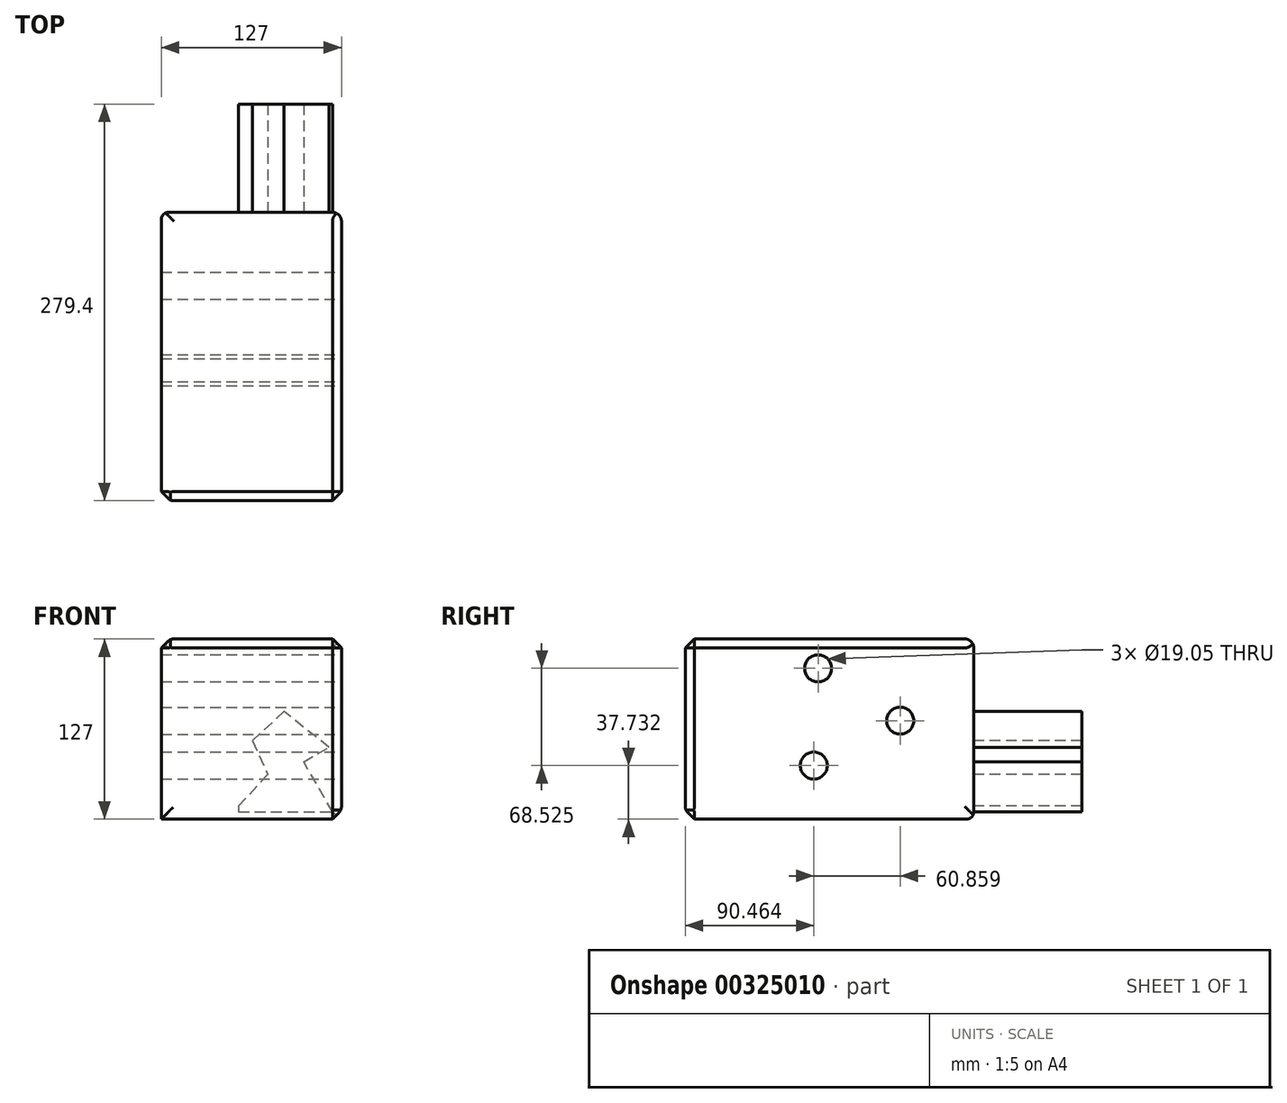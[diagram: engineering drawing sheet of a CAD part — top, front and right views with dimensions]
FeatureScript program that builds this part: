
annotation { "Feature Type Name" : "Feature", "Feature Type Description" : "" }
export const myFeature = defineFeature(function(context is Context, id is Id, definition is map)
    precondition{}
    {
        {
            var Q0;
            Q0=qCreatedBy(makeId("Front.planeOp"),FACE);
            var sketch = newSketch(context, id + "F0", { "sketchPlane" : qUnion([Q0])});
            skLineSegment(sketch, "E0.bottom", {"start": v(0, 0) * mm, "end": v(127, 0) * mm});
            skLineSegment(sketch, "E0.top", {"start": v(0, 127) * mm, "end": v(127, 127) * mm});
            skLineSegment(sketch, "E0.left", {"start": v(0, 0) * mm, "end": v(0, 127) * mm});
            skLineSegment(sketch, "E0.right", {"start": v(127, 0) * mm, "end": v(127, 127) * mm});
            skSolve(sketch);
        }
        {
            var Q0;
            Q0=makeQuery(id+"F0.imprint","IMPRINT",FACE,{"disambiguationData":[TD([[makeQuery(id+"F0.imprint","IMPRINT",EDGE,{"derivedFrom":sQuery(id+"F0.wireOp",EDGE,"E0.bottom")}),1.0]])]});
            extrude(context, id + "F1", {"entities" : qUnion([Q0]), "depth" : 203.2 * mm});
        }
        {
            var Q0;
            Q0=makeQuery(id+"F1.opExtrude","SWEPT_FACE",FACE,{"disambiguationData":[OSD([sQuery(id+"F0.wireOp",EDGE,"E0.right")])]});
            var sketch = newSketch(context, id + "F2", { "sketchPlane" : qUnion([Q0])});
            skCircle(sketch, "E1", {"center": v(-109.7, 106.26) * mm, "radius": 7.62 * mm});
            skCircle(sketch, "E2.1.0", {"center": v(-112.74, 37.73) * mm, "radius": 7.62 * mm});
            skCircle(sketch, "E2.2.0", {"center": v(-51.88, 69.37) * mm, "radius": 7.62 * mm});
            skPoint(sketch, "E2.center", {"position": v(-91.44, 71.12) * mm});
            skSolve(sketch);
        }
        {
            var Q0;
            Q0=sQuery(id+"F2.wireOp",VERTEX,"E1.center");
            var Q1;
            Q1=sQuery(id+"F2.wireOp",VERTEX,"E2.2.0.center");
            var Q2;
            Q2=sQuery(id+"F2.wireOp",VERTEX,"E2.1.0.center");
            var Q3;
            Q3=makeQuery(id+"F1.opExtrude","SWEPT_BODY",BODY,{"disambiguationData":[OSD([sQuery(id+"F0.wireOp",EDGE,"E0.bottom"),sQuery(id+"F0.wireOp",EDGE,"E0.top"),sQuery(id+"F0.wireOp",EDGE,"E0.left"),sQuery(id+"F0.wireOp",EDGE,"E0.right")])]});
            hole(context, id + "F3", {"style" : HoleStyle.SIMPLE, "endStyle" : HoleEndStyle.THROUGH, "holeDiameter" : 19.05 * mm, "tappedDepth" : 12.7 * mm, "tapClearance" : 3, "locations" : qUnion([Q0, Q1, Q2]), "scope" : qUnion([Q3])});
        }
        {
            var Q0;
            Q0=makeQuery(id+"F1.opExtrude","CAP_EDGE",EDGE,{"disambiguationData":[OSD([sQuery(id+"F0.wireOp",EDGE,"E0.top")])],"isStart":false});
            var Q1;
            Q1=makeQuery(id+"F1.opExtrude","CAP_EDGE",EDGE,{"disambiguationData":[OSD([sQuery(id+"F0.wireOp",EDGE,"E0.left")])],"isStart":false});
            var Q2;
            Q2=makeQuery(id+"F1.opExtrude","CAP_EDGE",EDGE,{"disambiguationData":[OSD([sQuery(id+"F0.wireOp",EDGE,"E0.right")])],"isStart":false});
            var Q3;
            Q3=makeQuery(id+"F1.opExtrude","CAP_EDGE",EDGE,{"disambiguationData":[OSD([sQuery(id+"F0.wireOp",EDGE,"E0.bottom")])],"isStart":false});
            var Q4;
            Q4=makeQuery(id+"F1.opExtrude","SWEPT_EDGE",EDGE,{"disambiguationData":[OSD([sQuery(id+"F0.wireOp",EDGE,"E0.bottom"),sQuery(id+"F0.wireOp",EDGE,"E0.right")])]});
            var Q5;
            Q5=makeQuery(id+"F1.opExtrude","SWEPT_EDGE",EDGE,{"disambiguationData":[OSD([sQuery(id+"F0.wireOp",EDGE,"E0.top"),sQuery(id+"F0.wireOp",EDGE,"E0.right")])]});
            var Q6;
            Q6=makeQuery(id+"F1.opExtrude","SWEPT_EDGE",EDGE,{"disambiguationData":[OSD([sQuery(id+"F0.wireOp",EDGE,"E0.top"),sQuery(id+"F0.wireOp",EDGE,"E0.left")])]});
            chamfer(context, id + "F4", {"entities" : qUnion([Q0, Q1, Q2, Q3, Q4, Q5, Q6]), "width" : 6.35 * mm, "tangentPropagation" : true});
        }
        {
            var Q0;
            {var subQ0=sQuery(id+"F0.wireOp",EDGE,"E0.top");Q0=makeQuery(id+"F4.opChamfer","BLEND_EDGE",EDGE,{"blendedFrom":[makeQuery(id+"F1.opExtrude","SWEPT_EDGE",EDGE,{"disambiguationData":[OSD([subQ0,sQuery(id+"F0.wireOp",EDGE,"E0.left")])]}),makeQuery(id+"F1.opExtrude","SWEPT_FACE",FACE,{"disambiguationData":[OSD([subQ0])]})],"blendedInto":[makeQuery(id+"F1.opExtrude","SWEPT_FACE",FACE,{"disambiguationData":[OSD([subQ0])]})]});}
            var Q1;
            Q1=makeQuery(id+"F1.opExtrude","CAP_EDGE",EDGE,{"disambiguationData":[OSD([sQuery(id+"F0.wireOp",EDGE,"E0.top")])],"isStart":true});
            var Q2;
            Q2=makeQuery(id+"F1.opExtrude","CAP_EDGE",EDGE,{"disambiguationData":[OSD([sQuery(id+"F0.wireOp",EDGE,"E0.right")])],"isStart":true});
            var Q3;
            {var subQ0=sQuery(id+"F0.wireOp",EDGE,"E0.right");Q3=makeQuery(id+"F4.opChamfer","BLEND_EDGE",EDGE,{"blendedFrom":[makeQuery(id+"F1.opExtrude","SWEPT_EDGE",EDGE,{"disambiguationData":[OSD([sQuery(id+"F0.wireOp",EDGE,"E0.bottom"),subQ0])]}),makeQuery(id+"F1.opExtrude","SWEPT_FACE",FACE,{"disambiguationData":[OSD([subQ0])]})],"blendedInto":[makeQuery(id+"F1.opExtrude","SWEPT_FACE",FACE,{"disambiguationData":[OSD([subQ0])]})]});}
            var Q4;
            Q4=makeQuery(id+"F3.hole-2.boolean.opBoolean","COPY",EDGE,{"derivedFrom":makeQuery(id+"F3.hole-2.opRevolve","SWEPT_EDGE",EDGE,{"disambiguationData":[OSD([sQuery(id+"F3.hole-2.sketch.wireOp",EDGE,"core_line_2"),sQuery(id+"F3.hole-2.sketch.wireOp",EDGE,"core_line_3")])]})});
            var Q5;
            Q5=makeQuery(id+"F3.hole-1.boolean.opBoolean","COPY",EDGE,{"derivedFrom":makeQuery(id+"F3.hole-1.opRevolve","SWEPT_EDGE",EDGE,{"disambiguationData":[OSD([sQuery(id+"F3.hole-1.sketch.wireOp",EDGE,"core_line_2"),sQuery(id+"F3.hole-1.sketch.wireOp",EDGE,"core_line_3")])]})});
            var Q6;
            Q6=makeQuery(id+"F3.hole-0.boolean.opBoolean","COPY",EDGE,{"derivedFrom":makeQuery(id+"F3.hole-0.opRevolve","SWEPT_EDGE",EDGE,{"disambiguationData":[OSD([sQuery(id+"F3.hole-0.sketch.wireOp",EDGE,"core_line_2"),sQuery(id+"F3.hole-0.sketch.wireOp",EDGE,"core_line_3")])]})});
            fillet(context, id + "F5", {"entities" : qUnion([Q0, Q1, Q2, Q3, Q4, Q5, Q6]), "radius" : 6.35 * mm, "tangentPropagation" : true, "allowEdgeOverflow" : false});
        }
        {
            var Q0;
            {var subQ0=sQuery(id+"F0.wireOp",EDGE,"E0.left");Q0=makeQuery(id+"F4.opChamfer","BLEND_EDGE",EDGE,{"blendedFrom":[makeQuery(id+"F1.opExtrude","CAP_EDGE",EDGE,{"disambiguationData":[OSD([subQ0])],"isStart":false}),makeQuery(id+"F1.opExtrude","CAP_FACE",FACE,{"disambiguationData":[OSD([sQuery(id+"F0.wireOp",EDGE,"E0.bottom"),sQuery(id+"F0.wireOp",EDGE,"E0.top"),subQ0,sQuery(id+"F0.wireOp",EDGE,"E0.right")])],"isStart":false})],"blendedInto":[makeQuery(id+"F1.opExtrude","CAP_FACE",FACE,{"disambiguationData":[OSD([sQuery(id+"F0.wireOp",EDGE,"E0.bottom"),sQuery(id+"F0.wireOp",EDGE,"E0.top"),subQ0,sQuery(id+"F0.wireOp",EDGE,"E0.right")])],"isStart":false})]});}
            var Q1;
            {var subQ0=sQuery(id+"F0.wireOp",EDGE,"E0.bottom");Q1=makeQuery(id+"F4.opChamfer","BLEND_EDGE",EDGE,{"blendedFrom":[makeQuery(id+"F1.opExtrude","CAP_EDGE",EDGE,{"disambiguationData":[OSD([subQ0])],"isStart":false}),makeQuery(id+"F1.opExtrude","CAP_FACE",FACE,{"disambiguationData":[OSD([subQ0,sQuery(id+"F0.wireOp",EDGE,"E0.top"),sQuery(id+"F0.wireOp",EDGE,"E0.left"),sQuery(id+"F0.wireOp",EDGE,"E0.right")])],"isStart":false})],"blendedInto":[makeQuery(id+"F1.opExtrude","CAP_FACE",FACE,{"disambiguationData":[OSD([subQ0,sQuery(id+"F0.wireOp",EDGE,"E0.top"),sQuery(id+"F0.wireOp",EDGE,"E0.left"),sQuery(id+"F0.wireOp",EDGE,"E0.right")])],"isStart":false})]});}
            fillet(context, id + "F6", {"entities" : qUnion([Q0, Q1]), "radius" : 5.08 * mm, "tangentPropagation" : true, "allowEdgeOverflow" : false});
        }
        {
            var Q0;
            Q0=makeQuery(id+"F1.opExtrude","CAP_EDGE",EDGE,{"disambiguationData":[OSD([sQuery(id+"F0.wireOp",EDGE,"E0.bottom")])],"isStart":true});
            var Q1;
            Q1=makeQuery(id+"F1.opExtrude","CAP_EDGE",EDGE,{"disambiguationData":[OSD([sQuery(id+"F0.wireOp",EDGE,"E0.left")])],"isStart":true});
            fillet(context, id + "F7", {"entities" : qUnion([Q0, Q1]), "radius" : 5.08 * mm, "tangentPropagation" : true, "allowEdgeOverflow" : false});
        }
        {
            var Q0;
            Q0=makeQuery(id+"F1.opExtrude","CAP_FACE",FACE,{"disambiguationData":[OSD([sQuery(id+"F0.wireOp",EDGE,"E0.bottom"),sQuery(id+"F0.wireOp",EDGE,"E0.top"),sQuery(id+"F0.wireOp",EDGE,"E0.left"),sQuery(id+"F0.wireOp",EDGE,"E0.right")])],"isStart":true});
            var sketch = newSketch(context, id + "F8", { "sketchPlane" : qUnion([Q0])});
            skLineSegment(sketch, "E3", {"start": v(-120.65, 5.08) * mm, "end": v(-100.43, 40.33) * mm});
            skLineSegment(sketch, "E4", {"start": v(-100.43, 40.33) * mm, "end": v(-118.28, 50.57) * mm});
            skLineSegment(sketch, "E5", {"start": v(-118.28, 50.57) * mm, "end": v(-86.5, 75.92) * mm});
            skLineSegment(sketch, "E6", {"start": v(-86.5, 75.92) * mm, "end": v(-64.17, 55.18) * mm});
            skLineSegment(sketch, "E7", {"start": v(-64.17, 55.18) * mm, "end": v(-75.2, 31.47) * mm});
            skLineSegment(sketch, "E8", {"start": v(-75.2, 31.47) * mm, "end": v(-54.43, 9.18) * mm});
            skLineSegment(sketch, "E9", {"start": v(-54.43, 9.18) * mm, "end": v(-54.43, 5.08) * mm});
            skLineSegment(sketch, "E10", {"start": v(-54.43, 5.08) * mm, "end": v(-120.65, 5.08) * mm});
            skSolve(sketch);
        }
        {
            var Q0;
            Q0=makeQuery(id+"F8.imprint","IMPRINT",FACE,{"disambiguationData":[TD([[makeQuery(id+"F8.imprint","IMPRINT",EDGE,{"derivedFrom":sQuery(id+"F8.wireOp",EDGE,"E3")}),-1.0]])]});
            extrude(context, id + "F9", {"entities" : qUnion([Q0]), "operationType" : NewBodyOperationType.ADD, "depth" : 76.2 * mm});
        }
    });
